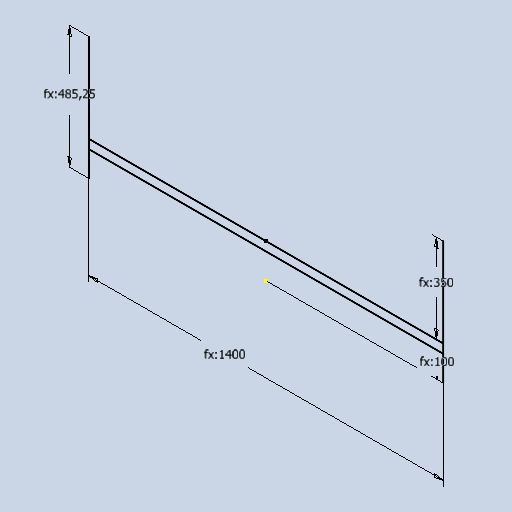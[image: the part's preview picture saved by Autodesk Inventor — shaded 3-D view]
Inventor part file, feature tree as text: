
AUTODESK INVENTOR PART (.ipt)
format: ipt  version: 2025 (Build 290162010, 162A)  size: 86,016 bytes
history: native  units: mm
features: sketch x1
ambient origin geometry x8: Origin, YZ Plane, XZ Plane, XY Plane, X Axis, Y Axis, Z Axis, Center Point
feature tree (1):
  sketch  "Sketch1"  dims[d0=485.249557mm d1=1400.0mm d2=100.0mm d4=350.0mm]
